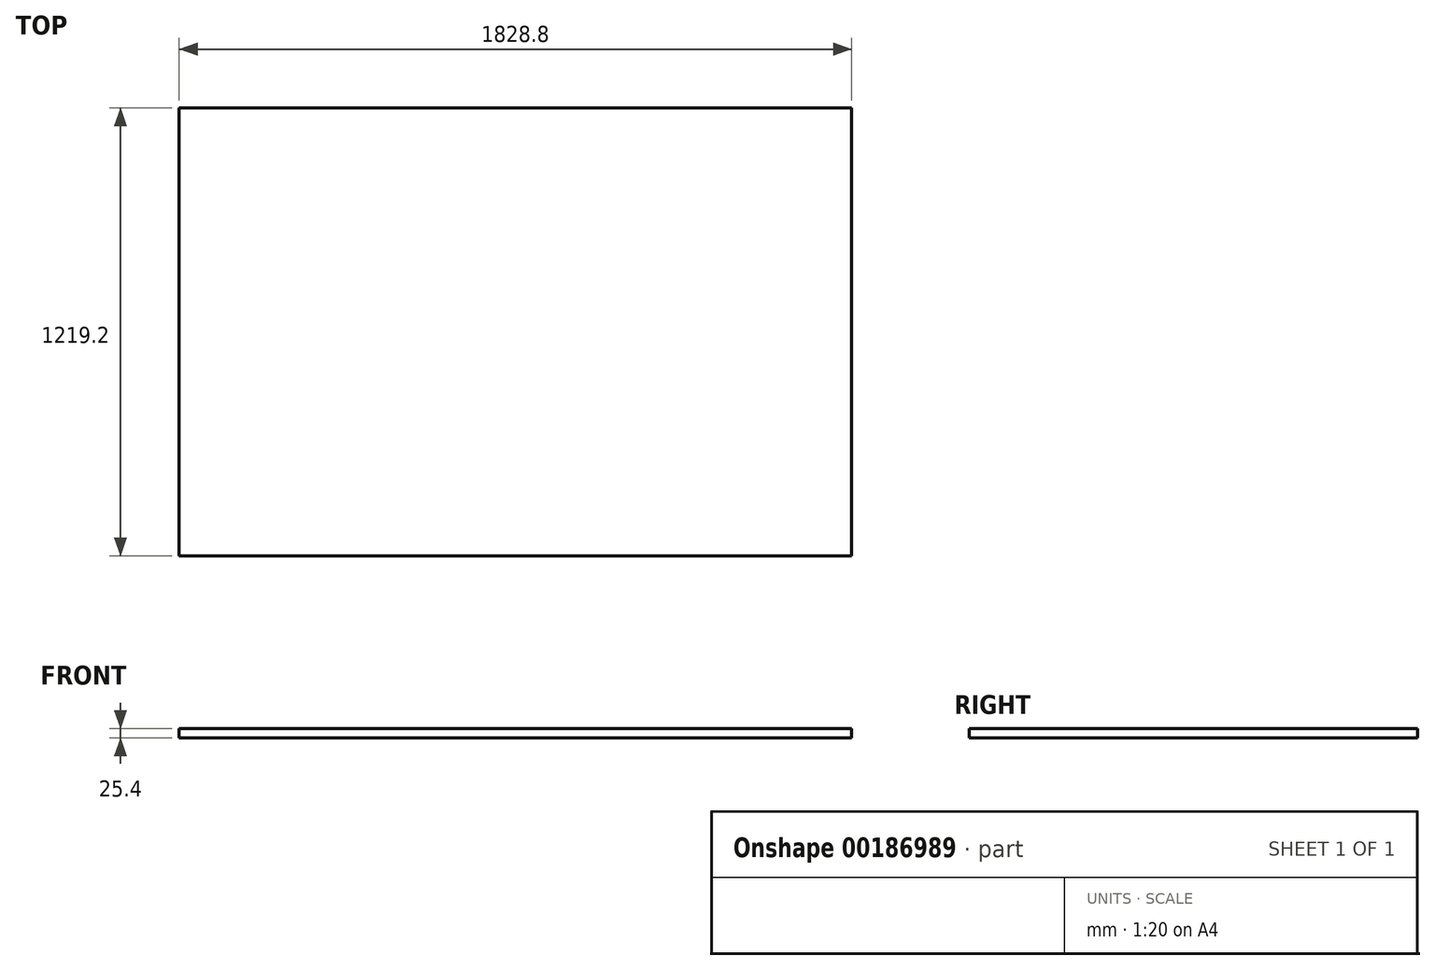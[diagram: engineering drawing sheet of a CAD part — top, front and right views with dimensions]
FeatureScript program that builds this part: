
annotation { "Feature Type Name" : "Feature", "Feature Type Description" : "" }
export const myFeature = defineFeature(function(context is Context, id is Id, definition is map)
    precondition{}
    {
        {
            var Q0;
            Q0=qCreatedBy(makeId("Top.planeOp"),FACE);
            var sketch = newSketch(context, id + "F0", { "sketchPlane" : qUnion([Q0])});
            skLineSegment(sketch, "E0.bottom", {"start": v(0, 0) * mm, "end": v(1828.8, 0) * mm});
            skLineSegment(sketch, "E0.top", {"start": v(0, 1219.2) * mm, "end": v(1828.8, 1219.2) * mm});
            skLineSegment(sketch, "E0.left", {"start": v(0, 0) * mm, "end": v(0, 1219.2) * mm});
            skLineSegment(sketch, "E0.right", {"start": v(1828.8, 0) * mm, "end": v(1828.8, 1219.2) * mm});
            skSolve(sketch);
        }
        {
            var Q0;
            Q0 = qSketchRegion(id + "F0", true);
            extrude(context, id + "F1", {"entities" : qUnion([Q0]), "depth" : 25.4 * mm});
        }
    });
